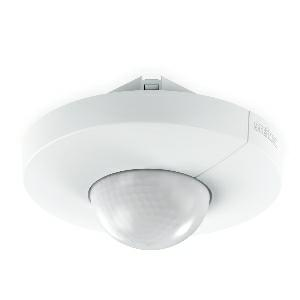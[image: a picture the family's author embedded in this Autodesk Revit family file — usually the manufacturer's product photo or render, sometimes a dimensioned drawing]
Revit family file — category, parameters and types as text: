
# Revit family: is_345_058289
name_source: partatom
category: Elektroinstallationen
revit_build: Autodesk Revit 2016 (Build: 20190508_0715(x64)
units: mm (PartAtom-declared; Revit-internal decimal feet)

## family parameters
Basisbauteil = Fläche
Beim Laden mit Abzugskörper schneiden = Nein
Bemaßung runder Anschluss = Durchmesser verwenden
Beschriftungsausrichtung beibehalten = Nein
Gemeinsam genutzt = Nein
Raumberechnungspunkt = Nein
Teiletyp = Normal

## types (1)
- IS 345
    Apparent Load = 0 VA
    Beschreibung = Type: Motion detectors; Dimensions (Ø x H): 124 x 78 mm; Sensor Technology: passive infrared; Application, place: Indoors; Application, room: corridor / aisle, multi-storey / underground car park, Indoors; Installation site: ceiling; Installation: Concealed wiring; Electronic scalability: No; Mechanical scalability: No; Mounting height: 2,50 – 5,00 m; Optimum mounting height: 2,5 m; Detection angle: 360 °; Angle of aperture: 45 °; Sneak-by guard: Yes; Capability of masking out individual segments: Yes; Reach, radial: 12 x 6 m (72 m²); Reach, tangential: 23 x 6 m (138 m²); Twilight setting TEACH: Yes; Time setting: 0 sec – 1092 min; Basic light level function: Yes; KNX functions: Photo-cell controller, Basic light level function, Light level, HVAC output, Constant-lighting control, Light output 2x, Presence output, Day / night function; With bus coupling: Yes; Settings via: ETS software, Remote control, Bus, Smart Remote; IP-rating: IP20; Material: Plastic; Colour: white; Version: KNX - concealed, rd.; PU1, EAN: 4007841058289
    Height = 0 mm  [stored 0 ft]
    Hersteller = Steinel
    Length = 124 mm  [stored 0.406824 ft]
    Maximum range = 11.589 m
    ModVariant = Nein
    Modell = 058289
    Mounting Place = Ceiling
    Mounting Type = Recessed
    Number of Poles = 1
    OnlyDefault = Ja
    Power Factor = 1
    Product Name = IS 345
    Product group = Presence detector
    ProductGroupID = 4
    Protection Class = Protection class
    Protection Degree = IP 20
    RlxData = <blob elided: 156049 chars, md5=13b61a45>
    Sensor characteristics = Stretched
    Sensor type = Passive (infrared)
    SensorDataFile = <blob elided: 5885 chars, md5=98bccc25>
    Type of entry = Motion
    Typenbild = produkt1_058289.jpg
    Typenkommentare = Product without accessories
    URL = http://relux.com
    VarID = ---
    Voltage = 0 V
    Vorgabe-Ansicht = 1800 mm
    Weight = 0.00 kg
    Width = 0 mm  [stored 0 ft]

note: [stored X ft] marks values corroborated as IEEE doubles in the binary element streams (Revit-internal decimal feet)

## geometry (parser evidence)
native form markers: Blend x4, Sweep x16
no freeform markers — native parametric forms only
